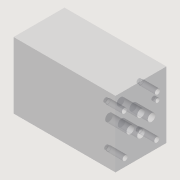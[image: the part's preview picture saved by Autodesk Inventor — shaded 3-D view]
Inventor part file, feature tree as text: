
AUTODESK INVENTOR PART (.ipt)
format: ipt  version: 2014 (Build 180170000, 170)  size: 372,736 bytes
history: native  units: mm
features: other x48, extrude x30, sketch x30
ambient origin geometry x8: Origin, YZ Plane, XZ Plane, XY Plane, X Axis, Y Axis, Z Axis, Center Point
bodies: 实体1 (feature_tree)
feature tree (108):
  extrude  "拉伸1"  Depth=200.0mm
  other  "UCS1"
  other  "UCS2"
  other  "UCS3"
  other  "UCS4"
  other  "UCS5"
  other  "UCS6"
  extrude  "拉伸2"  Depth=100.0mm
  extrude  "拉伸3"  Depth=4.25mm
  extrude  "拉伸4"  Depth=15.5mm
  extrude  "拉伸5"  TaperAngle=0.0deg  [1 undecoded]
  extrude  "拉伸6"  Depth=0.75mm
  extrude  "拉伸7"  Depth=31.75mm
  extrude  "拉伸8"  Depth=18.5mm
  extrude  "拉伸9"  Depth=18.5mm
  extrude  "拉伸10"  Depth=5.0mm
  extrude  "拉伸11"  Depth=16.0mm
  extrude  "拉伸12"  Depth=21.5mm
  extrude  "拉伸13"  Depth=12.7mm
  extrude  "拉伸14"  Depth=21.5mm
  extrude  "拉伸44"  Depth=30.2mm
  extrude  "拉伸45"  Depth=21.0mm
  extrude  "拉伸46"  Depth=21.0mm
  extrude  "拉伸47"  Depth=4.0mm
  extrude  "拉伸48"  Depth=33.0mm
  extrude  "拉伸49"  Depth=4.0mm
  extrude  "拉伸50"  TaperAngle=0.0deg  [1 undecoded]
  extrude  "拉伸51"  TaperAngle=0.0deg  [1 undecoded]
  extrude  "拉伸52"  Depth=43.0mm
  extrude  "拉伸53"  Depth=100.0mm
  extrude  "拉伸54"  Depth=100.0mm
  extrude  "拉伸55"  Depth=100.0mm
  extrude  "拉伸56"  Depth=100.0mm
  extrude  "拉伸57"  Depth=100.0mm
  extrude  "拉伸58"  Depth=100.0mm
  extrude  "拉伸59"  Depth=100.0mm
  sketch  "草图1"  dims[d0=65.0mm d1=0.0mm]
  sketch  "草图2"  dims[d2=0.0mm d3=0.0mm d4=0.0mm d5=0.0mm d6=0.0mm d7=0.0mm]
  sketch  "草图3"  dims[d8=0.0mm d9=0.0mm d10=0.0mm d11=0.0mm d12=0.0mm d13=0.0mm]
  sketch  "草图4"  dims[d14=0.0mm d15=0.0mm d16=0.0mm d17=0.0mm d18=0.0mm d19=0.0mm]
  sketch  "草图5"  dims[d20=0.0mm d21=0.0mm d22=0.0mm d23=0.0mm d24=0.0mm d25=0.0mm]
  sketch  "草图6"  dims[d26=0.0mm d27=0.0mm d28=0.0mm d29=0.0mm d30=0.0mm d31=0.0mm]
  sketch  "草图7"  dims[d32=0.0mm d33=0.0mm d34=0.0mm d35=0.0mm d36=0.0mm d37=0.0mm d38=200.0mm]
  sketch  "草图8"  dims[d39=100.0mm d40=43.0mm]
  sketch  "草图9"  dims[d41=51.0mm d42=4.25mm]
  sketch  "草图10"  dims[d43=21.5mm d44=15.5mm]
  sketch  "草图11"  dims[d45=31.0mm d46=0.0mm]
  sketch  "草图12"  dims[d47=40.5mm d48=0.75mm]
  sketch  "草图13"  dims[d49=40.5mm d50=31.75mm]
  sketch  "草图14"  dims[d51=18.5mm d52=0.0mm d53=18.5mm d54=-10.297443mm]
  sketch  "草图55"  dims[d55=18.5mm d56=-10.297443mm d57=18.5mm d58=-10.297443mm]
  sketch  "草图56"  dims[d59=18.5mm d60=-10.297443mm d61=5.0mm]
  sketch  "草图57"  dims[d62=16.0mm d63=0.0mm d64=7.5mm]
  sketch  "草图58"  dims[d67=25.9mm d68=21.5mm]
  sketch  "草图59"  dims[d69=15.5mm d70=12.7mm]
  sketch  "草图60"  dims[d71=5.1mm d72=21.5mm]
  sketch  "草图61"  dims[d73=15.5mm d74=30.2mm]
  sketch  "草图62"  dims[d75=21.0mm d76=0.0mm d77=21.0mm d78=-10.297443mm]
  sketch  "草图63"  dims[d79=21.0mm d80=-10.297443mm d81=21.0mm d82=-10.297443mm]
  sketch  "草图64"  dims[d83=21.0mm d84=-10.297443mm d85=4.0mm]
  sketch  "草图65"  dims[d86=31.75mm d87=33.0mm]
  sketch  "草图66"  dims[d88=4.0mm d89=0.0mm d90=4.0mm d91=-10.297443mm]
  sketch  "草图67"  dims[d105=0.0mm d119=0.0mm]
  sketch  "草图68"  dims[d125=0.0mm d131=0.0mm]
  sketch  "草图69"  dims[d135=0.0mm d267=43.0mm]
  sketch  "草图70"  dims[d268=51.0mm d269=29.0mm d270=25.0mm d271=21.5mm d272=15.5mm d273=4.25mm d274=0.75mm d275=40.5mm d276=40.5mm d277=31.75mm d278=0.0mm d279=31.0mm d280=18.5mm d281=0.0mm d282=18.5mm d283=-10.297443mm d284=18.5mm d285=-10.297443mm d286=18.5mm d287=-10.297443mm d288=18.5mm d289=-10.297443mm d290=5.0mm d291=16.0mm d292=0.0mm d293=7.5mm d294=21.5mm d295=5.1mm d296=21.0mm d297=0.0mm d298=21.0mm d299=-10.297443mm d300=7.5mm d301=12.7mm d302=15.5mm d303=19.0mm d304=0.0mm d305=19.0mm d306=-10.297443mm d307=7.5mm d308=15.5mm d309=30.2mm d310=20.0mm d311=0.0mm d312=20.0mm d313=-10.297443mm d314=7.5mm d315=25.9mm d316=21.5mm d317=18.0mm d318=0.0mm d319=18.0mm d320=-10.297443mm d321=4.0mm d322=33.0mm d323=31.75mm d324=4.0mm d325=0.0mm d326=4.0mm d327=-10.297443mm d328=50.0mm d329=100.0mm]
  other  "UCS1: YZ 平面"
  other  "UCS1: XZ 平面"
  other  "UCS1: XY 平面"
  other  "UCS1: X 轴"
  other  "UCS1: Y 轴"
  other  "UCS1: Z 轴"
  other  "UCS1: 原点"
  other  "UCS2: YZ 平面"
  other  "UCS2: XZ 平面"
  other  "UCS2: XY 平面"
  other  "UCS2: X 轴"
  other  "UCS2: Y 轴"
  other  "UCS2: Z 轴"
  other  "UCS2: 原点"
  other  "UCS3: YZ 平面"
  other  "UCS3: XZ 平面"
  other  "UCS3: XY 平面"
  other  "UCS3: X 轴"
  other  "UCS3: Y 轴"
  other  "UCS3: Z 轴"
  other  "UCS3: 原点"
  other  "UCS4: YZ 平面"
  other  "UCS4: XZ 平面"
  other  "UCS4: XY 平面"
  other  "UCS4: X 轴"
  other  "UCS4: Y 轴"
  other  "UCS4: Z 轴"
  other  "UCS4: 原点"
  other  "UCS5: YZ 平面"
  other  "UCS5: XZ 平面"
  other  "UCS5: XY 平面"
  other  "UCS5: X 轴"
  other  "UCS5: Y 轴"
  other  "UCS5: Z 轴"
  other  "UCS5: 原点"
  other  "UCS6: YZ 平面"
  other  "UCS6: XZ 平面"
  other  "UCS6: XY 平面"
  other  "UCS6: X 轴"
  other  "UCS6: Y 轴"
  other  "UCS6: Z 轴"
  other  "UCS6: 原点"
note: 3 required parameter values undecoded (feature->parameter linkage not recoverable at this tier; creation-order binding heuristic only, values carry confidence <= 0.55)
